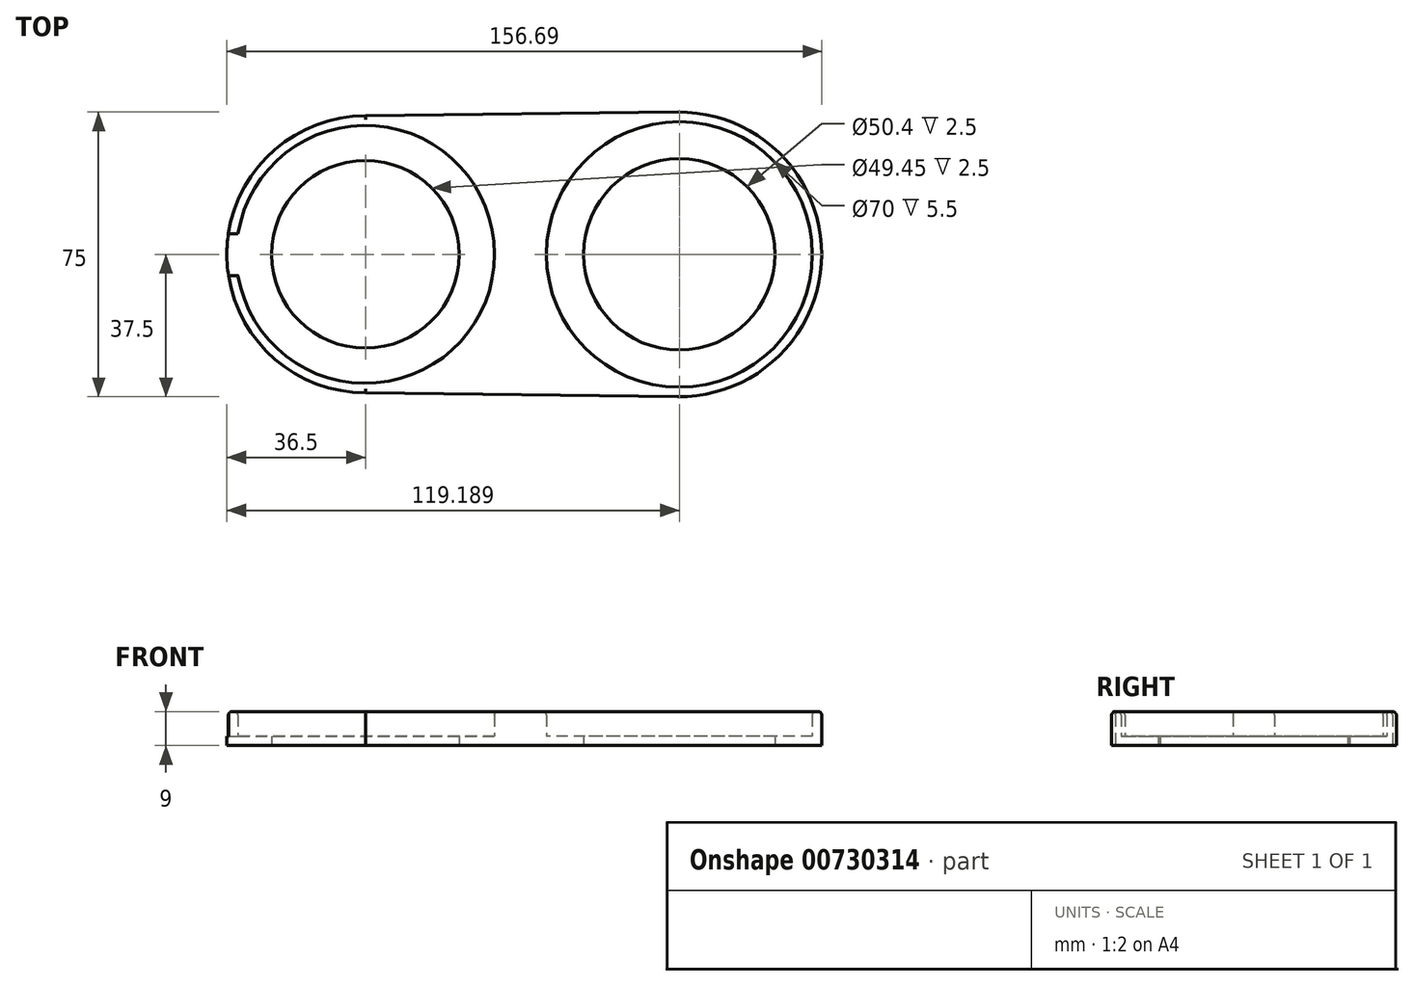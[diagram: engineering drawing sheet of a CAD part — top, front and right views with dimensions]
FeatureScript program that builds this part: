
annotation { "Feature Type Name" : "Feature", "Feature Type Description" : "" }
export const myFeature = defineFeature(function(context is Context, id is Id, definition is map)
    precondition{}
    {
        {
            var Q0;
            Q0=qCreatedBy(makeId("Top.planeOp"),FACE);
            var sketch = newSketch(context, id + "F0", { "sketchPlane" : qUnion([Q0])});
            skCircle(sketch, "E0", {"center": v(0, 0) * mm, "radius": 34 * mm});
            skCircle(sketch, "E1", {"center": v(0, 0) * mm, "radius": 36.5 * mm});
            skCircle(sketch, "E2", {"center": v(82.69, 0) * mm, "radius": 35 * mm});
            skCircle(sketch, "E3", {"center": v(82.69, 0) * mm, "radius": 37.5 * mm});
            skLineSegment(sketch, "E4", {"start": v(0, 36.5) * mm, "end": v(82.23, 37.5) * mm});
            skLineSegment(sketch, "E5", {"start": v(0, -36.5) * mm, "end": v(82.23, -37.5) * mm});
            skCircle(sketch, "E6", {"center": v(0, 0) * mm, "radius": 24.72 * mm});
            skCircle(sketch, "E7", {"center": v(82.69, 0) * mm, "radius": 25.2 * mm});
            skSolve(sketch);
        }
        {
            var Q0;
            {var subQ0=sQuery(id+"F0.wireOp",EDGE,"E4");Q0=makeQuery(id+"F0.imprint","IMPRINT",FACE,{"disambiguationData":[TD([[makeQuery(id+"F0.imprint","IMPRINT",EDGE,{"derivedFrom":subQ0}),-1.0]])]});}
            var Q1;
            Q1=makeQuery(id+"F0.imprint","IMPRINT",FACE,{"disambiguationData":[TD([[makeQuery(id+"F0.imprint","IMPRINT",EDGE,{"derivedFrom":sQuery(id+"F0.wireOp",EDGE,"E0")}),-1.0]])]});
            var Q2;
            Q2=makeQuery(id+"F0.imprint","IMPRINT",FACE,{"disambiguationData":[TD([[makeQuery(id+"F0.imprint","IMPRINT",EDGE,{"derivedFrom":sQuery(id+"F0.wireOp",EDGE,"E0")}),1.0]])]});
            var Q3;
            Q3=makeQuery(id+"F0.imprint","IMPRINT",FACE,{"disambiguationData":[TD([[makeQuery(id+"F0.imprint","IMPRINT",EDGE,{"derivedFrom":sQuery(id+"F0.wireOp",EDGE,"E2")}),1.0]])]});
            var Q4;
            Q4=makeQuery(id+"F0.imprint","IMPRINT",FACE,{"disambiguationData":[TD([[makeQuery(id+"F0.imprint","IMPRINT",EDGE,{"derivedFrom":sQuery(id+"F0.wireOp",EDGE,"E2")}),-1.0]])]});
            extrude(context, id + "F1", {"entities" : qUnion([Q0, Q1, Q2, Q3, Q4]), "depth" : 2.5 * mm, "offsetDistance" : 25 * mm});
        }
        {
            var Q0;
            Q0 = qSketchRegion(id + "F0", true);
            extrude(context, id + "F2", {"entities" : qUnion([Q0]), "operationType" : NewBodyOperationType.ADD, "depth" : 9 * mm, "offsetDistance" : 25 * mm});
        }
        {
            var Q0;
            Q0=makeQuery(id+"F2.opExtrude","CAP_EDGE",EDGE,{"disambiguationData":[OSD([sQuery(id+"F0.wireOp",EDGE,"E0")])],"isStart":false});
            var Q1;
            Q1=makeQuery(id+"F2.opExtrude","CAP_EDGE",EDGE,{"disambiguationData":[OSD([sQuery(id+"F0.wireOp",EDGE,"E2")])],"isStart":false});
            var Q2;
            Q2=makeQuery(id+"F2.opExtrude","CAP_FACE",FACE,{"disambiguationData":[OSD([sQuery(id+"F0.wireOp",EDGE,"E0"),sQuery(id+"F0.wireOp",EDGE,"E1"),sQuery(id+"F0.wireOp",EDGE,"E2"),sQuery(id+"F0.wireOp",EDGE,"E3"),sQuery(id+"F0.wireOp",EDGE,"E4"),sQuery(id+"F0.wireOp",EDGE,"E5")])],"isStart":false});
            fillet(context, id + "F3", {"entities" : qUnion([Q0, Q1, Q2]), "radius" : 1 * mm, "tangentPropagation" : true, "allowEdgeOverflow" : false});
        }
        {
            var Q0;
            Q0=qCreatedBy(makeId("Right.planeOp"),FACE);
            var sketch = newSketch(context, id + "F4", { "sketchPlane" : qUnion([Q0])});
            skLineSegment(sketch, "E8.bottom", {"start": v(-5.58, 2.5) * mm, "end": v(5.42, 2.5) * mm});
            skLineSegment(sketch, "E8.top", {"start": v(-5.58, 12.21) * mm, "end": v(5.42, 12.21) * mm});
            skLineSegment(sketch, "E8.left", {"start": v(-5.58, 2.5) * mm, "end": v(-5.58, 12.21) * mm});
            skLineSegment(sketch, "E8.right", {"start": v(5.42, 2.5) * mm, "end": v(5.42, 12.21) * mm});
            skSolve(sketch);
        }
        {
            var Q0;
            Q0=makeQuery(id+"F4.imprint","IMPRINT",FACE,{"disambiguationData":[TD([[makeQuery(id+"F4.imprint","IMPRINT",EDGE,{"derivedFrom":sQuery(id+"F4.wireOp",EDGE,"E8.bottom")}),1.0]])]});
            extrude(context, id + "F5", {"entities" : qUnion([Q0]), "operationType" : NewBodyOperationType.REMOVE, "oppositeDirection" : true, "depth" : 100 * mm, "offsetDistance" : 25 * mm});
        }
    });
